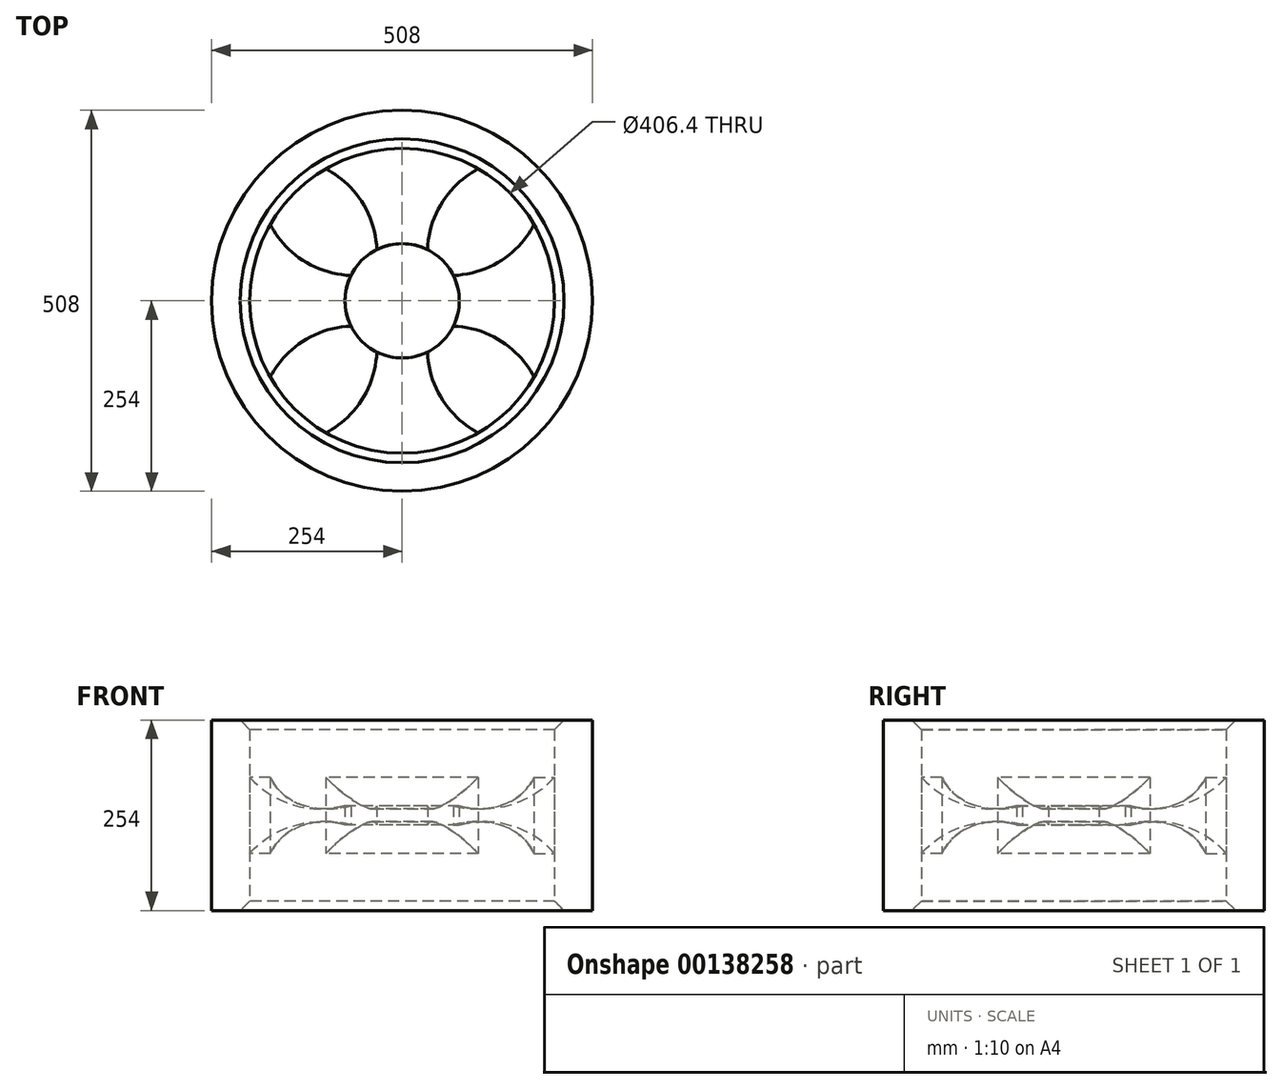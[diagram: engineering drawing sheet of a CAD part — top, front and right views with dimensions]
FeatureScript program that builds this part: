
annotation { "Feature Type Name" : "Feature", "Feature Type Description" : "" }
export const myFeature = defineFeature(function(context is Context, id is Id, definition is map)
    precondition{}
    {
        {
            var Q0;
            Q0=qCreatedBy(makeId("Top.planeOp"),FACE);
            var sketch = newSketch(context, id + "F4", { "sketchPlane" : qUnion([Q0])});
            skCircle(sketch, "E0", {"center": v(0, 0) * mm, "radius": 203.2 * mm});
            skCircle(sketch, "E1.0", {"center": v(0, 0) * mm, "radius": 254 * mm});
            skLineSegment(sketch, "E2", {"start": v(0, 0) * mm, "end": v(0, 203.2) * mm, "construction": true});
            skCircle(sketch, "E3", {"center": v(0, 0) * mm, "radius": 76.2 * mm});
            skLineSegment(sketch, "E4", {"start": v(76.2, 0) * mm, "end": v(-76.2, 0) * mm, "construction": true});
            skArc(sketch, "E5", {"start": v(-50.8, 0) * mm, "mid": v(-38.72, 98.8) * mm, "end": v(-101.6, 175.98) * mm});
            skArc(sketch, "E6.MirrorCS", {"start": v(50.8, 0) * mm, "mid": v(38.72, 98.8) * mm, "end": v(101.6, 175.98) * mm});
            skSolve(sketch);
        }
        {
            var Q0;
            Q0=makeQuery(id+"F4.imprint","IMPRINT",FACE,{"disambiguationData":[TD([[makeQuery(id+"F4.imprint","IMPRINT",EDGE,{"derivedFrom":sQuery(id+"F4.wireOp",EDGE,"E1.0")}),1.0]])]});
            extrude(context, id + "F5", {"entities" : qUnion([Q0]), "depth" : 127 * mm, "hasSecondDirection" : true, "secondDirectionOppositeDirection" : true, "secondDirectionDepth" : 127 * mm});
        }
        {
            var Q0;
            {var subQ0=sQuery(id+"F4.wireOp",EDGE,"E3");var subQ1=makeQuery(id+"F4.imprint","INTERSECT",VERTEX,{"derivedFrom":[subQ0,sQuery(id+"F4.wireOp",EDGE,"E5")]});Q0=makeQuery(id+"F4.imprint","IMPRINT",FACE,{"disambiguationData":[TD([[makeQuery(id+"F4.imprint","IMPRINT",EDGE,{"disambiguationData":[TD([[subQ1,1.0]])],"derivedFrom":subQ0}),1.0]])]});}
            extrude(context, id + "F0", {"entities" : qUnion([Q0]), "depth" : 12.7 * mm, "hasSecondDirection" : true, "secondDirectionOppositeDirection" : true, "secondDirectionDepth" : 12.7 * mm});
        }
        {
            var Q0;
            {var subQ0=sQuery(id+"F4.wireOp",EDGE,"E5");var subQ1=sQuery(id+"F4.wireOp",EDGE,"E0");var subQ2=makeQuery(id+"F4.imprint","INTERSECT",VERTEX,{"derivedFrom":[subQ1,subQ0]});Q0=makeQuery(id+"F4.imprint","IMPRINT",FACE,{"disambiguationData":[TD([[makeQuery(id+"F4.imprint","IMPRINT",EDGE,{"disambiguationData":[TD([[subQ2,1.0]])],"derivedFrom":subQ1}),1.0]])]});}
            extrude(context, id + "F1", {"entities" : qUnion([Q0]), "depth" : 76.2 * mm, "hasSecondDirection" : true, "secondDirectionOppositeDirection" : true, "secondDirectionDepth" : 76.2 * mm});
        }
        {
            var Q0;
            Q0=qCreatedBy(makeId("Right.planeOp"),FACE);
            var sketch = newSketch(context, id + "F2", { "sketchPlane" : qUnion([Q0])});
            skLineSegment(sketch, "E7.0", {"start": v(-76.2, 0) * mm, "end": v(76.2, 0) * mm});
            skLineSegment(sketch, "E8.0", {"start": v(-203.2, 0) * mm, "end": v(203.2, 0) * mm});
            skLineSegment(sketch, "E9.bottom", {"start": v(76.2, 76.2) * mm, "end": v(203.2, 76.2) * mm});
            skLineSegment(sketch, "E9.top", {"start": v(76.2, -76.2) * mm, "end": v(203.2, -76.2) * mm});
            skLineSegment(sketch, "E9.left", {"start": v(76.2, 76.2) * mm, "end": v(76.2, -76.2) * mm});
            skLineSegment(sketch, "E9.right", {"start": v(203.2, 76.2) * mm, "end": v(203.2, -76.2) * mm});
            skArc(sketch, "E10", {"start": v(76.2, 12.7) * mm, "mid": v(145.07, 13.86) * mm, "end": v(203.2, 50.8) * mm});
            skArc(sketch, "E11", {"start": v(203.2, -50.8) * mm, "mid": v(145.07, -13.86) * mm, "end": v(76.2, -12.7) * mm});
            skLineSegment(sketch, "E12", {"start": v(0, 0) * mm, "end": v(0, -78.4) * mm});
            skSolve(sketch);
        }
        {
            var Q0;
            {var subQ0=sQuery(id+"F2.wireOp",EDGE,"E9.bottom");Q0=makeQuery(id+"F2.imprint","IMPRINT",FACE,{"disambiguationData":[TD([[makeQuery(id+"F2.imprint","IMPRINT",EDGE,{"derivedFrom":subQ0}),-1.0]])]});}
            var Q1;
            {var subQ0=sQuery(id+"F2.wireOp",EDGE,"E9.top");Q1=makeQuery(id+"F2.imprint","IMPRINT",FACE,{"disambiguationData":[TD([[makeQuery(id+"F2.imprint","IMPRINT",EDGE,{"derivedFrom":subQ0}),1.0]])]});}
            var Q2;
            Q2=sQuery(id+"F2.wireOp",EDGE,"E12");
            revolve(context, id + "F6", {"operationType" : NewBodyOperationType.REMOVE, "entities" : qUnion([Q0, Q1]), "axis" : qUnion([Q2]), "revolveType" : RevolveType.FULL, "oppositeDirection" : true});
        }
        {
            var Q0;
            Q0=makeQuery(id+"F1.opExtrude","SWEPT_BODY",BODY,{"disambiguationData":[OSD([sQuery(id+"F4.wireOp",EDGE,"E0"),sQuery(id+"F4.wireOp",EDGE,"E3"),sQuery(id+"F4.wireOp",EDGE,"E5"),sQuery(id+"F4.wireOp",EDGE,"E6.MirrorCS")])]});
            var Q1;
            Q1=makeQuery(id+"F0.opExtrude","CAP_EDGE",EDGE,{"disambiguationData":[OSD([sQuery(id+"F4.wireOp",EDGE,"E3")])],"isStart":false});
            circularPattern(context, id + "F7", {"entities" : qUnion([Q0]), "axis" : qUnion([Q1]), "angle" : 90 * degree, "instanceCount" : 4});
        }
        {
            var Q0;
            Q0=makeQuery(id+"F5.opExtrude","CAP_EDGE",EDGE,{"disambiguationData":[OSD([sQuery(id+"F4.wireOp",EDGE,"E0")])],"isStart":true});
            var Q1;
            Q1=makeQuery(id+"F5.opExtrude","CAP_EDGE",EDGE,{"disambiguationData":[OSD([sQuery(id+"F4.wireOp",EDGE,"E0")])],"isStart":false});
            chamfer(context, id + "F3", {"entities" : qUnion([Q0, Q1]), "width" : 12.7 * mm, "tangentPropagation" : true});
        }
    });
